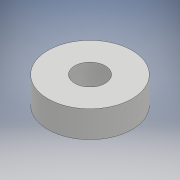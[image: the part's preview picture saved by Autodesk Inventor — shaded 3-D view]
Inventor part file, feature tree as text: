
AUTODESK INVENTOR PART (.ipt)
format: ipt  version: 2017 SP1 (Build 210196100, 196)  size: 94,720 bytes
history: native  units: mm
features: extrude x1, sketch x1
ambient origin geometry x8: Origin, YZ Plane, XZ Plane, XY Plane, X Axis, Y Axis, Z Axis, Center Point
bodies: Solide1 (feature_tree)
feature tree (2):
  extrude  "Extrusion1"  Depth=8.0mm
  sketch  "Esquisse1"
